# Revit family: Sanitary_Taps-And-Mixers_Sanindusa_Unit_Urinal-Electronic-Tap-Powred-By-Battery-Unit
name_source: partatom
category: Plumbing Fixtures
revit_build: Autodesk Revit 2018 (Build: 20170223_1515(x64)
units: mm (PartAtom-declared; Revit-internal decimal feet)

## family parameters
Cut with Voids When Loaded = No
Host = Face
Part Type = Normal
Room Calculation Point = No
Round Connector Dimension = Use Diameter
Shared = No

## types (1)
- Sanitary_Taps-And-Mixers_Sanindusa_Unit_Urinal-Electronic-Tap-Powred-By-Battery-Unit
    AssetType = Fixed
    BodyMaterial = stainless steel
    Color = Brushed stainless steel
    Constituents = "1x Plastic box with conceled flush valve;
1x Wall cover plate with electronic sensor;
1x Plastic seat for the cover plate;
1x Temporary protective cover;
4x Screws;
1x Allen key."
    Default Elevation = 1219 mm
    Description = A small diameter valve, with a free outlet, from which water is drawn.
    Element Type = FAUCET: A small diameter valve, with a free outlet, from which water is drawn.
    FaucetFunction = Cold
    FaucetOperation = TimedSelfClosing
    FaucetTopDescription = Eletronic tap
    FaucetType = Other
    Features = The electronic taps have sensors which allows for the good management of this precious commodity. The simplicity and easiness in how it is used are two great advantages. Promotes water saving, avoids bacteria and virus proliferation.
    Finish = Brushed stainless steel
    FlowCoefficient = water flow to 3 bar: 6.0L/min.
    FlowRateMaximum = water flow to 3 bar: 6.0L/min.
    InletConnectionType = G 1/2"
    Installation Instructions = https://www.tec.sanindusa.pt
    InstallationDate = 1900-12-31T23:59:59
    Manufacturer = Sanindusa
    ManufacturerName = Sanindusa
    ManufacturerURL = www.tec.sanindusa.pt
    Material = stainless steel
    Model = 5410571
    ModelNumber = 5410571
    ModelReference = Unit
    Name = Urinal electronic tap powred by battery unit
    NominalHeight = 140 mm  [stored 0.459318 ft]
    NominalLength = 140 mm  [stored 0.459318 ft]
    NominalWidth = 6 mm  [stored 0.019685 ft]
    OutletConnectionType = G 1/2"
    Pre-defined type (IFC) = FAUCET
    ProductInformation = https://www.tec.sanindusa.pt
    ProductionYear = 2019
    Size = 140x6x140
    TestPressure = 10 bar
    Type (IFC) = IfcValveType
    URL = www.tec.sanindusa.pt
    Uniclass2015Version = Products v1.6
    ValveMechanism = UNSET
    ValveOperation = SOLENOID
    ValvePattern = UNSET
    Version = 1
    WarrantyDescription = https://www.tec.sanindusa.pt
    WarrantyDurationParts = 5
    WarrantyDurationUnit = year
    WarrantyStartDate = 1900-12-31T23:59:59
    Weight = 1.13 kg
    WorkingPressure = 0.3-8.0 bar

note: [stored X ft] marks values corroborated as IEEE doubles in the binary element streams (Revit-internal decimal feet)

## geometry (parser evidence)
native form markers: Sweep x7
no freeform markers — native parametric forms only
